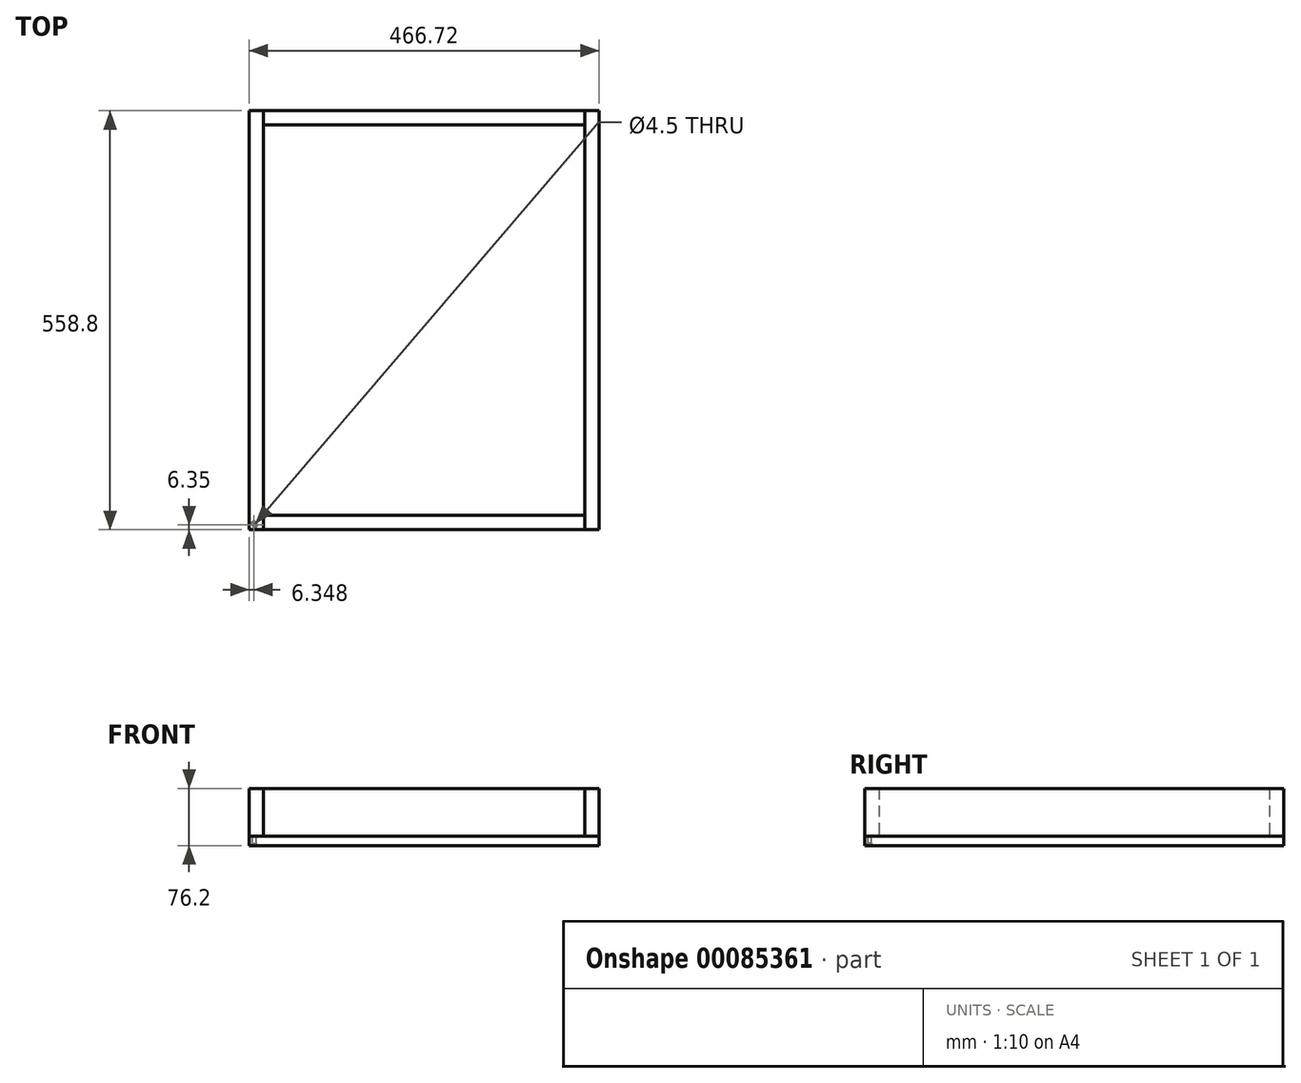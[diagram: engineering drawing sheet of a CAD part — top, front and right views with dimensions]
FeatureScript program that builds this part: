
annotation { "Feature Type Name" : "Feature", "Feature Type Description" : "" }
export const myFeature = defineFeature(function(context is Context, id is Id, definition is map)
    precondition{}
    {
        {
            var Q0;
            Q0=qCreatedBy(makeId("Top.planeOp"),FACE);
            var sketch = newSketch(context, id + "F0", { "sketchPlane" : qUnion([Q0])});
            skLineSegment(sketch, "E0.bottom", {"start": v(233.36, 279.4) * mm, "end": v(-233.36, 279.4) * mm});
            skLineSegment(sketch, "E0.top", {"start": v(233.36, -279.4) * mm, "end": v(-233.36, -279.4) * mm});
            skLineSegment(sketch, "E0.left", {"start": v(233.36, 279.4) * mm, "end": v(233.36, -279.4) * mm});
            skLineSegment(sketch, "E0.right", {"start": v(-233.36, 279.4) * mm, "end": v(-233.36, -279.4) * mm});
            skPoint(sketch, "E0.middle", {"position": v(0, 0) * mm});
            skSolve(sketch);
        }
        {
            var Q0;
            Q0=makeQuery(id+"F0.imprint","IMPRINT",FACE,{"disambiguationData":[TD([[makeQuery(id+"F0.imprint","IMPRINT",EDGE,{"derivedFrom":sQuery(id+"F0.wireOp",EDGE,"E0.bottom")}),1.0]])]});
            extrude(context, id + "F1", {"entities" : qUnion([Q0]), "depth" : 12.7 * mm});
        }
        {
            var Q0;
            Q0=makeQuery(id+"F1.opExtrude","CAP_FACE",FACE,{"disambiguationData":[OSD([sQuery(id+"F0.wireOp",EDGE,"E0.bottom"),sQuery(id+"F0.wireOp",EDGE,"E0.top"),sQuery(id+"F0.wireOp",EDGE,"E0.left"),sQuery(id+"F0.wireOp",EDGE,"E0.right")])],"isStart":false});
            var sketch = newSketch(context, id + "F2", { "sketchPlane" : qUnion([Q0])});
            skLineSegment(sketch, "E1.bottom", {"start": v(-233.36, -279.4) * mm, "end": v(-214.31, -279.4) * mm});
            skLineSegment(sketch, "E1.top", {"start": v(-233.36, 279.4) * mm, "end": v(-214.31, 279.4) * mm});
            skLineSegment(sketch, "E1.left", {"start": v(-233.36, -279.4) * mm, "end": v(-233.36, 279.4) * mm});
            skLineSegment(sketch, "E1.right", {"start": v(-214.31, -279.4) * mm, "end": v(-214.31, 279.4) * mm});
            skLineSegment(sketch, "E2.bottom", {"start": v(233.36, -279.4) * mm, "end": v(214.31, -279.4) * mm});
            skLineSegment(sketch, "E2.top", {"start": v(233.36, 279.4) * mm, "end": v(214.31, 279.4) * mm});
            skLineSegment(sketch, "E2.left", {"start": v(233.36, -279.4) * mm, "end": v(233.36, 279.4) * mm});
            skLineSegment(sketch, "E2.right", {"start": v(214.31, -279.4) * mm, "end": v(214.31, 279.4) * mm});
            skSolve(sketch);
        }
        {
            var Q0;
            Q0=makeQuery(id+"F2.imprint","IMPRINT",FACE,{"disambiguationData":[TD([[makeQuery(id+"F2.imprint","IMPRINT",EDGE,{"derivedFrom":sQuery(id+"F2.wireOp",EDGE,"E1.bottom")}),-1.0]])]});
            var Q1;
            Q1=makeQuery(id+"F2.imprint","IMPRINT",FACE,{"disambiguationData":[TD([[makeQuery(id+"F2.imprint","IMPRINT",EDGE,{"derivedFrom":sQuery(id+"F2.wireOp",EDGE,"E2.bottom")}),-1.0]])]});
            extrude(context, id + "F3", {"entities" : qUnion([Q0, Q1]), "depth" : 63.5 * mm});
        }
        {
            var Q0;
            Q0=makeQuery(id+"F1.opExtrude","CAP_FACE",FACE,{"disambiguationData":[OSD([sQuery(id+"F0.wireOp",EDGE,"E0.bottom"),sQuery(id+"F0.wireOp",EDGE,"E0.top"),sQuery(id+"F0.wireOp",EDGE,"E0.left"),sQuery(id+"F0.wireOp",EDGE,"E0.right")])],"isStart":false});
            var sketch = newSketch(context, id + "F4", { "sketchPlane" : qUnion([Q0])});
            skLineSegment(sketch, "E3.bottom", {"start": v(-214.31, 260.35) * mm, "end": v(214.31, 260.35) * mm});
            skLineSegment(sketch, "E3.top", {"start": v(-214.31, 279.4) * mm, "end": v(214.31, 279.4) * mm});
            skLineSegment(sketch, "E3.left", {"start": v(-214.31, 260.35) * mm, "end": v(-214.31, 279.4) * mm});
            skLineSegment(sketch, "E3.right", {"start": v(214.31, 260.35) * mm, "end": v(214.31, 279.4) * mm});
            skLineSegment(sketch, "E4.bottom", {"start": v(-214.31, -279.4) * mm, "end": v(214.31, -279.4) * mm});
            skLineSegment(sketch, "E4.top", {"start": v(-214.31, -260.35) * mm, "end": v(214.31, -260.35) * mm});
            skLineSegment(sketch, "E4.left", {"start": v(-214.31, -279.4) * mm, "end": v(-214.31, -260.35) * mm});
            skLineSegment(sketch, "E4.right", {"start": v(214.31, -279.4) * mm, "end": v(214.31, -260.35) * mm});
            skSolve(sketch);
        }
        {
            var Q0;
            Q0=makeQuery(id+"F4.imprint","IMPRINT",FACE,{"disambiguationData":[TD([[makeQuery(id+"F4.imprint","IMPRINT",EDGE,{"derivedFrom":sQuery(id+"F4.wireOp",EDGE,"E4.bottom")}),-1.0]])]});
            var Q1;
            Q1=makeQuery(id+"F4.imprint","IMPRINT",FACE,{"disambiguationData":[TD([[makeQuery(id+"F4.imprint","IMPRINT",EDGE,{"derivedFrom":sQuery(id+"F4.wireOp",EDGE,"E3.bottom")}),1.0]])]});
            var Q2;
            Q2=makeQuery(id+"F3.opExtrude","CAP_FACE",FACE,{"disambiguationData":[OSD([sQuery(id+"F2.wireOp",EDGE,"E1.bottom"),sQuery(id+"F2.wireOp",EDGE,"E1.top"),sQuery(id+"F2.wireOp",EDGE,"E1.left"),sQuery(id+"F2.wireOp",EDGE,"E1.right")])],"isStart":false});
            extrude(context, id + "F5", {"entities" : qUnion([Q0, Q1]), "endBound" : BoundingType.UP_TO_SURFACE, "endBoundEntityFace" : qUnion([Q2]), "depth" : 25.4 * mm});
        }
        {
            var Q0;
            Q0=makeQuery(id+"F1.opExtrude","CAP_FACE",FACE,{"disambiguationData":[OSD([sQuery(id+"F0.wireOp",EDGE,"E0.bottom"),sQuery(id+"F0.wireOp",EDGE,"E0.top"),sQuery(id+"F0.wireOp",EDGE,"E0.left"),sQuery(id+"F0.wireOp",EDGE,"E0.right")])],"isStart":true});
            var sketch = newSketch(context, id + "F6", { "sketchPlane" : qUnion([Q0])});
            skPoint(sketch, "E5", {"position": v(-227.01, 273.05) * mm});
            skSolve(sketch);
        }
        {
            var Q0;
            Q0=sQuery(id+"F6.wireOp",VERTEX,"E5");
            var Q1;
            Q1=makeQuery(id+"F1.opExtrude","SWEPT_BODY",BODY,{"disambiguationData":[OSD([sQuery(id+"F0.wireOp",EDGE,"E0.bottom"),sQuery(id+"F0.wireOp",EDGE,"E0.top"),sQuery(id+"F0.wireOp",EDGE,"E0.left"),sQuery(id+"F0.wireOp",EDGE,"E0.right")])]});
            hole(context, id + "F7", {"style" : HoleStyle.C_SINK, "endStyle" : HoleEndStyle.THROUGH, "standardTappedOrClearance" : lookupTablePath({ "standard" : "ANSI", "fit" : "Normal (ASME)", "size" : "#8", "type" : "Clearance" }), "standardBlindInLast" : lookupTablePath({ "fit" : "Free", "standard" : "ANSI", "size" : "#8", "type" : "Clearance" }), "holeDiameter" : 4.5 * mm, "cSinkDiameter" : 9.12 * mm, "cSinkAngle" : 82 * degree, "locations" : qUnion([Q0]), "scope" : qUnion([Q1]), "isTappedThrough" : true});
        }
        {
            var Q0;
            Q0=makeQuery(id+"F5.opExtrude","SWEPT_FACE",FACE,{"disambiguationData":[OSD([sQuery(id+"F4.wireOp",EDGE,"E3.top")])]});
            var sketch = newSketch(context, id + "F8", { "sketchPlane" : qUnion([Q0])});
            skLineSegment(sketch, "E6", {"start": v(0, 76.2) * mm, "end": v(0, 0) * mm});
            skPoint(sketch, "E7", {"position": v(0, 0) * mm});
            skSolve(sketch);
        }
    });
